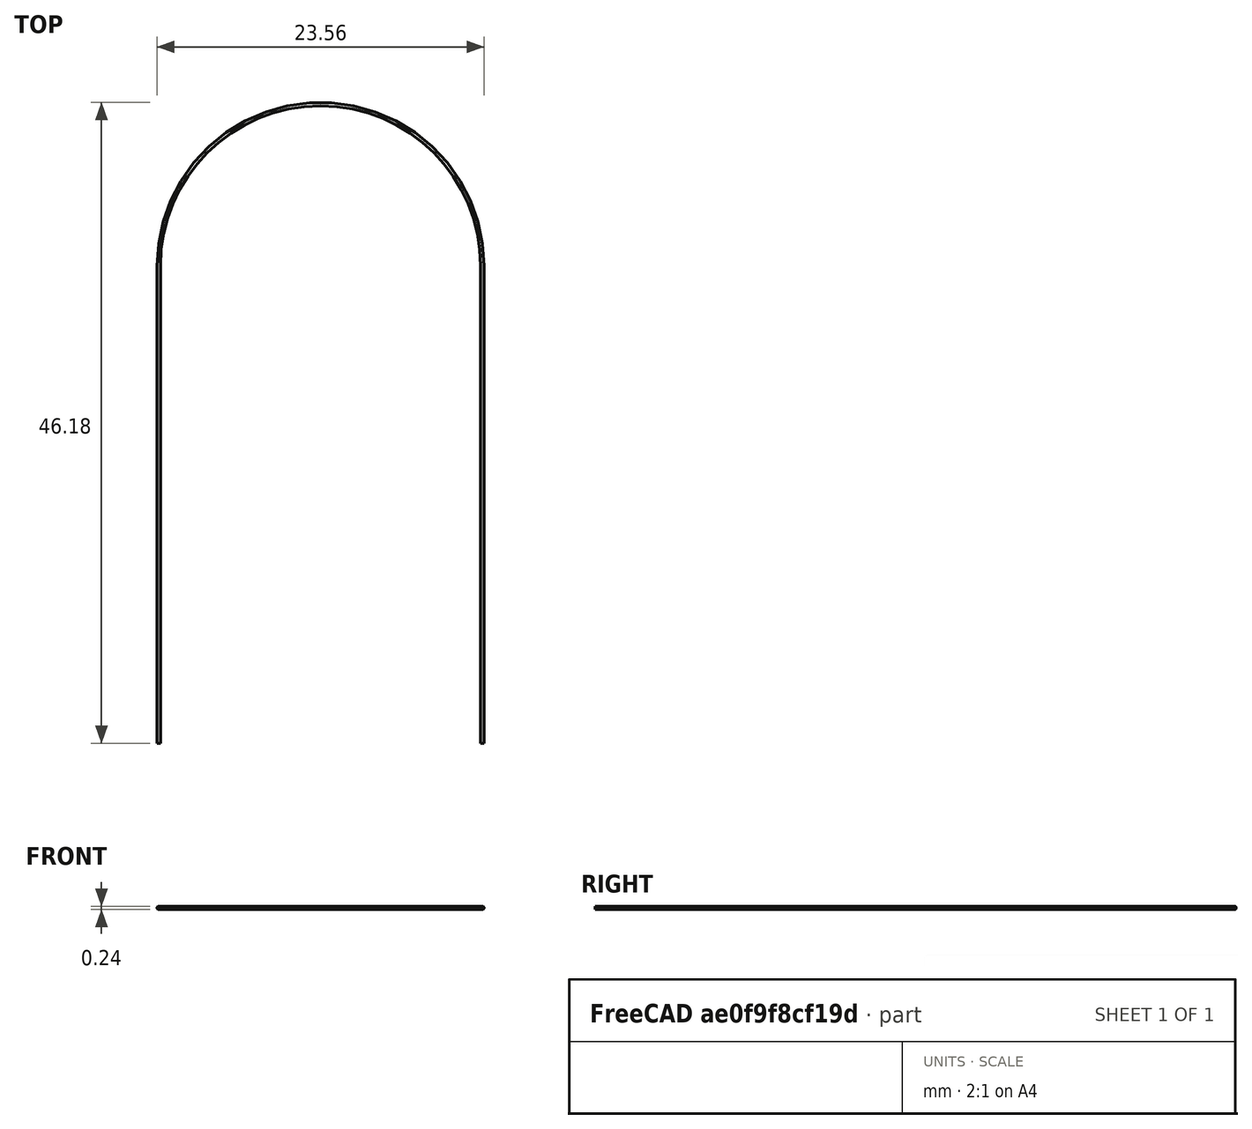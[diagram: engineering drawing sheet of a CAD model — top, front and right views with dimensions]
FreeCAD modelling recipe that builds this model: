
FCSTD DOCUMENT  (FreeCAD 1.2R20251119 (Git shallow))
Label: paper clip
License: All rights reserved
LicenseURL: https://en.wikipedia.org/wiki/All_rights_reserved
objects: Sketcher::SketchObject×2, App::Point×1, PartDesign::AdditivePipe×1, PartDesign::Body×1
note: 8 computed .brp shape members not serialized (recipe doc carries the construction recipe); baked Part::Feature solids carry a one-line shape summary decoded from their .brp

FEATURE [App::Point] Origin001
  Role = Origin
FEATURE [Sketcher::SketchObject] Sketch
  ArcFitTolerance = 1e-06
  AttachmentSupport = -> [Origin]
  ExternalTypes = [0]
  FullyConstrained = false
  MakeInternals = false
  MapMode = 5
  sketch-geometry (3):
    g0: ArcOfCircle CenterX=21.8496 CenterY=34.4004 CenterZ=0 NormalX=0 NormalY=0 NormalZ=1 AngleXU=0 Radius=11.6763 StartAngle=1.61e-14 EndAngle=3.14159
    g1: LineSegment StartX=10.1733 StartY=-1.4e-15 StartZ=0 EndX=10.1733 EndY=34.4004 EndZ=0
    g2: LineSegment StartX=33.5259 StartY=1.883e-13 StartZ=0 EndX=33.5259 EndY=34.4004 EndZ=0
  constraints (3):
    c: Tangent(g0,g1) = 1.5708
    c: Tangent(g0,g2) = -1.5708
    c: Vertical(g1)
FEATURE [Sketcher::SketchObject] Sketch001
  ArcFitTolerance = 1e-06
  AttachmentSupport = -> [Origin]
  ExternalTypes = [0]
  FullyConstrained = false
  MakeInternals = false
  MapMode = 5
  Placement = pos=(0,0,0) rot=(1,0,0;1.5708rad)
  sketch-geometry (1):
    g0: Circle CenterX=10.1925 CenterY=0 CenterZ=0 NormalX=0 NormalY=0 NormalZ=1 AngleXU=0 Radius=0.12033
  constraints (1):
    c: PointOnObject(g0,g-1)
FEATURE [PartDesign::AdditivePipe] AdditivePipe
  AuxiliaryCurvilinear = true
  AuxiliarySpineTangent = false
  Binormal = (0,0,0)
  Mode = 0
  Profile = -> Sketch001
  Refine = true
  Spine = -> Sketch
  SpineTangent = false
  Suppressed = false
  Transformation = 0
  Transition = 0
FEATURE [PartDesign::Body] Body
  AllowCompound = true
  Group = -> [Sketch,Sketch001,AdditivePipe]
  Origin = -> Origin
  Tip = -> AdditivePipe
